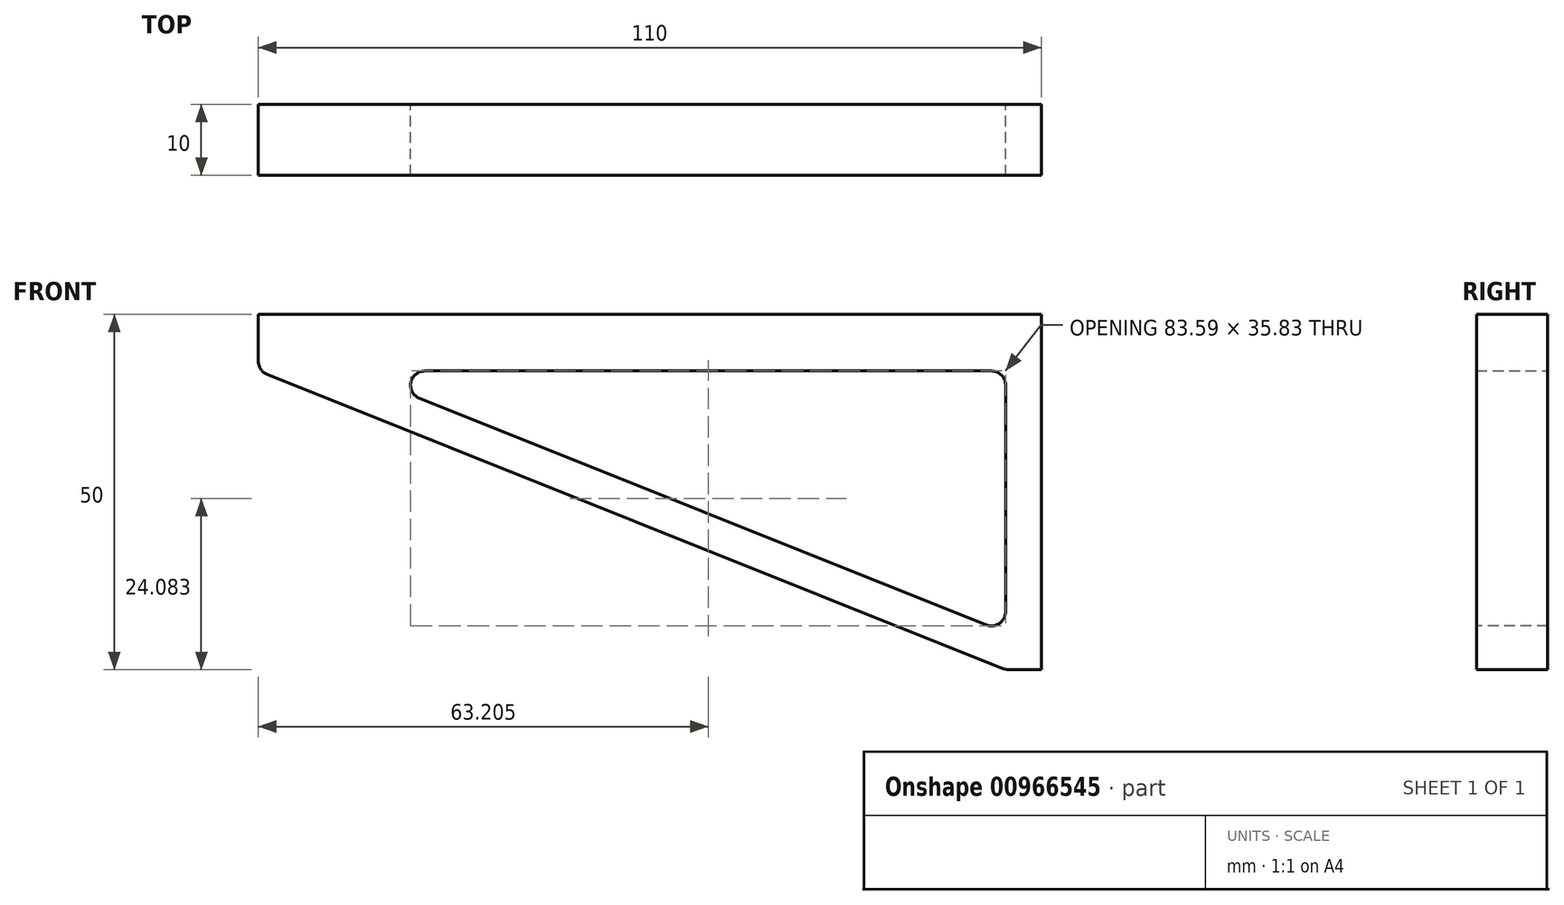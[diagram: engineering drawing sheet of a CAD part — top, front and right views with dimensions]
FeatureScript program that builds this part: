
annotation { "Feature Type Name" : "Feature", "Feature Type Description" : "" }
export const myFeature = defineFeature(function(context is Context, id is Id, definition is map)
    precondition{}
    {
        {
            var Q0;
            Q0=qCreatedBy(makeId("Front.planeOp"),FACE);
            var sketch = newSketch(context, id + "F0", { "sketchPlane" : qUnion([Q0])});
            skLineSegment(sketch, "E0", {"start": v(0, 0) * mm, "end": v(0, 50) * mm});
            skLineSegment(sketch, "E1", {"start": v(0, 50) * mm, "end": v(-110, 50) * mm});
            skLineSegment(sketch, "E2", {"start": v(-110, 50) * mm, "end": v(-110, 42) * mm});
            skLineSegment(sketch, "E3", {"start": v(0, 0) * mm, "end": v(-5, 0) * mm});
            skLineSegment(sketch, "E4", {"start": v(-5, 0) * mm, "end": v(-110, 42) * mm});
            skLineSegment(sketch, "E5", {"start": v(-110, 42) * mm, "end": v(-97, 42) * mm});
            skLineSegment(sketch, "E6", {"start": v(-97, 42) * mm, "end": v(-5, 5.2) * mm});
            skLineSegment(sketch, "E7", {"start": v(-5, 5.2) * mm, "end": v(-5, 42) * mm});
            skLineSegment(sketch, "E8", {"start": v(-97, 42) * mm, "end": v(-5, 42) * mm});
            skSolve(sketch);
        }
        {
            var Q0;
            Q0 = qSketchRegion(id + "F0", true);
            extrude(context, id + "F1", {"entities" : qUnion([Q0]), "depth" : 10 * mm, "offsetDistance" : 25 * mm});
        }
        {
            var Q0;
            Q0=makeQuery(id+"F1.opExtrude","SWEPT_EDGE",EDGE,{"disambiguationData":[OSD([sQuery(id+"F0.wireOp",EDGE,"E6"),sQuery(id+"F0.wireOp",EDGE,"E8")])]});
            var Q1;
            Q1=makeQuery(id+"F1.opExtrude","SWEPT_EDGE",EDGE,{"disambiguationData":[OSD([sQuery(id+"F0.wireOp",EDGE,"E6"),sQuery(id+"F0.wireOp",EDGE,"E7")])]});
            var Q2;
            Q2=makeQuery(id+"F1.opExtrude","SWEPT_EDGE",EDGE,{"disambiguationData":[OSD([sQuery(id+"F0.wireOp",EDGE,"E7"),sQuery(id+"F0.wireOp",EDGE,"E8")])]});
            var Q3;
            Q3=makeQuery(id+"F1.opExtrude","SWEPT_EDGE",EDGE,{"disambiguationData":[OSD([sQuery(id+"F0.wireOp",EDGE,"E2"),sQuery(id+"F0.wireOp",EDGE,"E4")])]});
            var Q4;
            Q4=makeQuery(id+"F1.opExtrude","SWEPT_EDGE",EDGE,{"disambiguationData":[OSD([sQuery(id+"F0.wireOp",EDGE,"E3"),sQuery(id+"F0.wireOp",EDGE,"E4")])]});
            fillet(context, id + "F2", {"entities" : qUnion([Q0, Q1, Q2, Q3, Q4]), "radius" : 2 * mm, "tangentPropagation" : true, "allowEdgeOverflow" : false});
        }
    });
